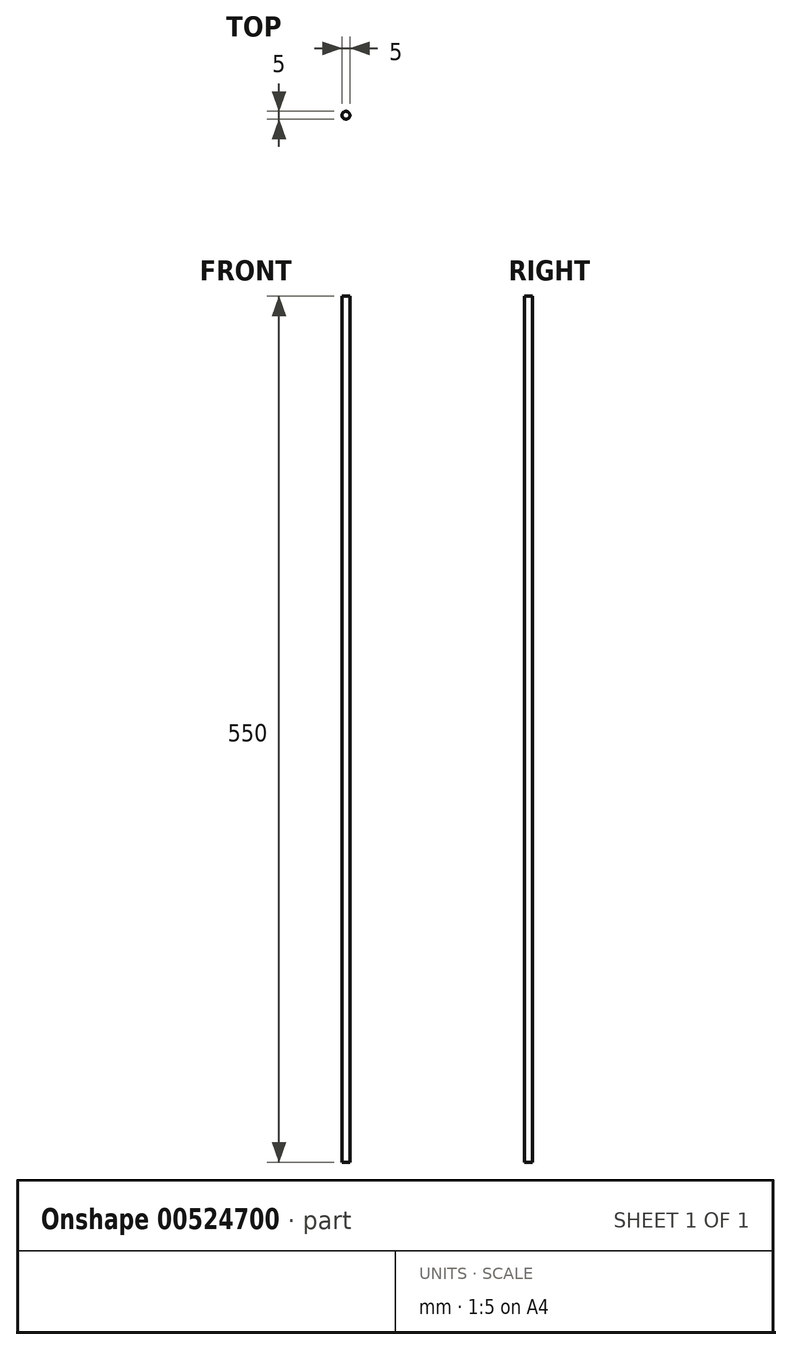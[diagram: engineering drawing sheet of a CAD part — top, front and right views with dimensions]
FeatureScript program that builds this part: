
annotation { "Feature Type Name" : "Feature", "Feature Type Description" : "" }
export const myFeature = defineFeature(function(context is Context, id is Id, definition is map)
    precondition{}
    {
        {
            var Q0;
            Q0=qCreatedBy(makeId("Top.planeOp"),FACE);
            var sketch = newSketch(context, id + "F0", { "sketchPlane" : qUnion([Q0])});
            skCircle(sketch, "E0", {"center": v(0, 0) * mm, "radius": 2.5 * mm});
            skSolve(sketch);
        }
        {
            var Q0;
            Q0=makeQuery(id+"F0.imprint","IMPRINT",FACE,{"disambiguationData":[TD([[makeQuery(id+"F0.imprint","IMPRINT",EDGE,{"derivedFrom":sQuery(id+"F0.wireOp",EDGE,"E0")}),1.0]])]});
            extrude(context, id + "F1", {"entities" : qUnion([Q0]), "depth" : 550 * mm, "offsetDistance" : 25 * mm});
        }
    });
